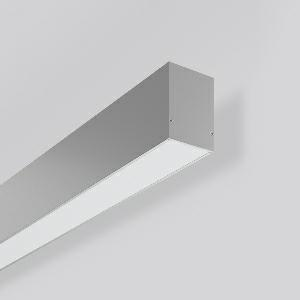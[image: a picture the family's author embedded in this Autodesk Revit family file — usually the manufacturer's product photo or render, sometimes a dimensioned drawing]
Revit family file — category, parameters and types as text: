
# Revit family: less_is_more_50_312607_0045_1_136a
name_source: partatom
category: Lighting Fixtures
units: mm (PartAtom-declared; Revit-internal decimal feet)

## family parameters
Cut with Voids When Loaded = No
Host = Face
Light Source = No
Part Type = Normal
Room Calculation Point = No
Round Connector Dimension = Use Diameter
Shared = No

## types (1)
- LESS IS MORE 50 (1 x LED Modul 840, 1500 lm, 4000)
    Apparent Load = 12 VA
    CIE Flux Codes = 48 80 96 100 100
    Color Rendering = 80
    Color Temperature = 4000
    Default Elevation = 1800 mm
    Description = Series: LESS IS MORE 50
Linear wall luminaires. Housing: extruded aluminium profile, powder-coated. End cap aluminium powder-coated. Diffuser made of non-yellowing plastic (PMMA), opal. Direct light emission. Suitable for Wall (surface). LED unit with integrated converter interchangeable and removable. Suitable for through-wiring. With sensors or as a safety luminaire on request. 
Colour: white aluminium (RAL 9006)
Length: 1127 mm
Width: 67 mm
Height: 75 mm
Lamp: LED
Socket: without socket
Colour temperature: 4000K
Colour rendering index (CRI): 80
System power: 12 W
Rated luminous flux: 1500 lm
Luminous efficiency: 125 lm/W
Control gear: Regulated power supply
Protection class: I
Type of protection: IP 20
    Height = 75 mm
    Lamp = 1 x LED Modul 840
    Lamp Light Flux = 1500 lm
    Lamp count = 1
    Length = 1127 mm
    Lifetime = 50000 h
    Luminous efficacy = 125 lm/W
    Manufacturer = RZB
    ModVariant = No
    Model = 312607.0045.1
    Mounting Place = Wall
    Mounting Type = Surface mounted
    Number of Poles = 1
    OnlyDefault = Yes
    Power Factor = 1
    Product Name = LESS IS MORE 50
    Product group = Surface mounted LED linear luminaires
    ProductGroupID = 2007
    Protection Class = Protection class I
    Protection Degree = IP 20
    RLX_Detail_Level = 1
    RLX_Emergency_Light_Flux = 0 lm
    RLX_Emergency_Type = 0
    RLX_Emergency_Type_DB = No
    RlxData = <blob elided: 38765 chars, md5=e9bce48b>
    Socket = socket
    Standby Power = 0 W
    System Light Flux = 1500 lm
    System Power = 12 W
    Type Comments = Product without accessories
    Type Image = 312606.0045.jpg
    URL = http://relux.com
    VarID = ---
    Voltage = 0 V
    Weight = 0.00 kg
    Width = 67 mm

## geometry (parser evidence)
native form markers: Blend x4, Sweep x10
no freeform markers — native parametric forms only
